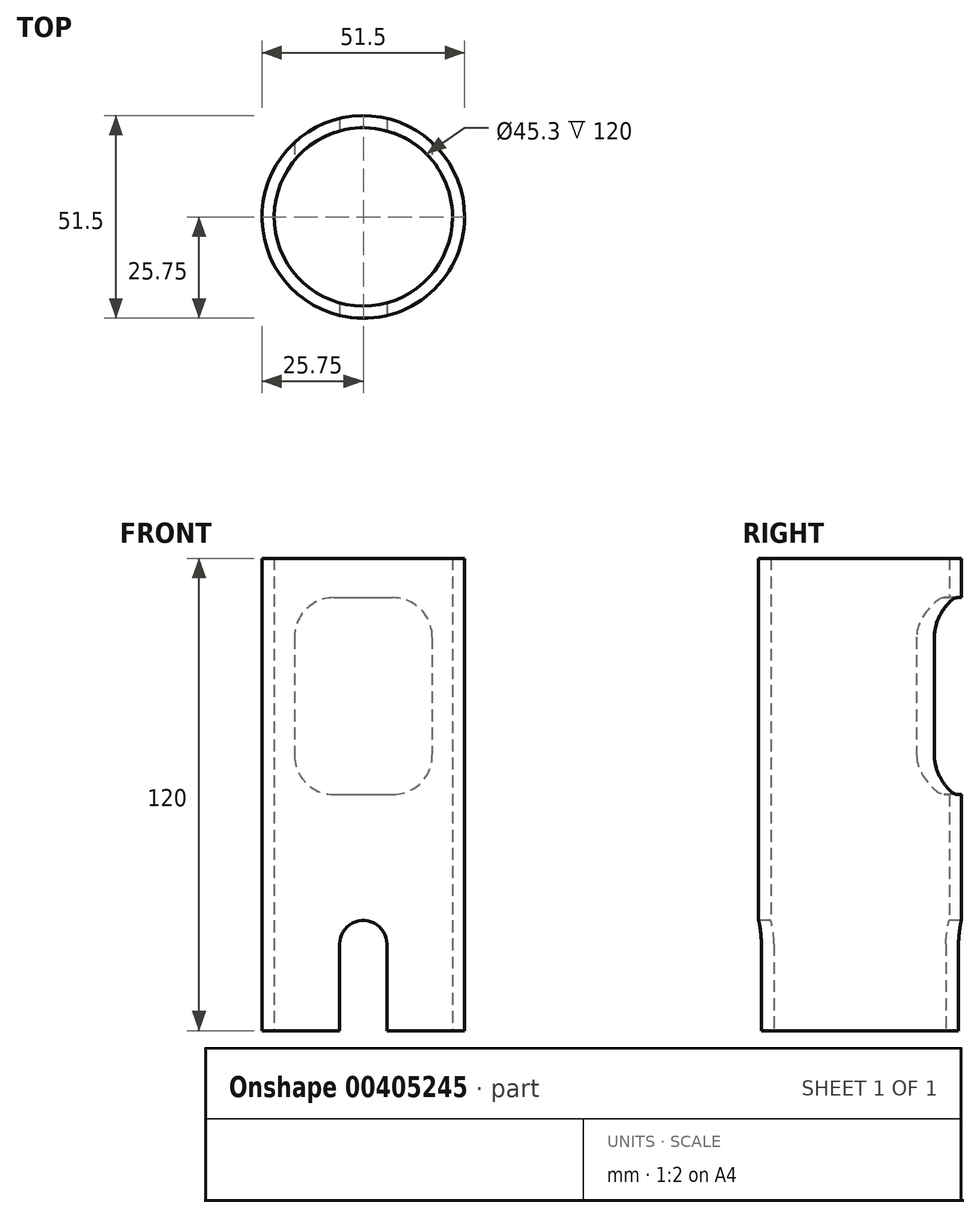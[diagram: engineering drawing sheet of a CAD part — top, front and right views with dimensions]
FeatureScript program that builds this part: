
annotation { "Feature Type Name" : "Feature", "Feature Type Description" : "" }
export const myFeature = defineFeature(function(context is Context, id is Id, definition is map)
    precondition{}
    {
        {
            var Q0;
            Q0=qCreatedBy(makeId("Top.planeOp"),FACE);
            var sketch = newSketch(context, id + "F0", { "sketchPlane" : qUnion([Q0])});
            skCircle(sketch, "E0", {"center": v(0, 0) * mm, "radius": 22.65 * mm});
            skCircle(sketch, "E1", {"center": v(0, 0) * mm, "radius": 25.75 * mm});
            skSolve(sketch);
        }
        {
            var Q0;
            Q0=makeQuery(id+"F0.imprint","IMPRINT",FACE,{"disambiguationData":[TD([[makeQuery(id+"F0.imprint","IMPRINT",EDGE,{"derivedFrom":sQuery(id+"F0.wireOp",EDGE,"E0")}),-1.0]])]});
            extrude(context, id + "F1", {"entities" : qUnion([Q0]), "depth" : 120 * mm});
        }
        {
            var Q0;
            Q0=qCreatedBy(makeId("Front.planeOp"),FACE);
            var sketch = newSketch(context, id + "F2", { "sketchPlane" : qUnion([Q0])});
            skLineSegment(sketch, "E2.bottom", {"start": v(-7.5, 110) * mm, "end": v(7.5, 110) * mm});
            skLineSegment(sketch, "E2.top", {"start": v(-7.5, 60) * mm, "end": v(7.5, 60) * mm});
            skLineSegment(sketch, "E2.left", {"start": v(-17.5, 100) * mm, "end": v(-17.5, 70) * mm});
            skLineSegment(sketch, "E2.right", {"start": v(17.5, 100) * mm, "end": v(17.5, 70) * mm});
            skPoint(sketch, "E3.visualSharp", {"position": v(-17.5, 110) * mm});
            skArc(sketch, "E3.filletArc", {"start": v(-7.5, 110) * mm, "mid": v(-14.57, 107.07) * mm, "end": v(-17.5, 100) * mm});
            skPoint(sketch, "E4.visualSharp", {"position": v(17.5, 110) * mm});
            skArc(sketch, "E4.filletArc", {"start": v(17.5, 100) * mm, "mid": v(14.57, 107.07) * mm, "end": v(7.5, 110) * mm});
            skPoint(sketch, "E5.visualSharp", {"position": v(17.5, 60) * mm});
            skArc(sketch, "E5.filletArc", {"start": v(7.5, 60) * mm, "mid": v(14.57, 62.93) * mm, "end": v(17.5, 70) * mm});
            skPoint(sketch, "E6.visualSharp", {"position": v(-17.5, 60) * mm});
            skArc(sketch, "E6.filletArc", {"start": v(-17.5, 70) * mm, "mid": v(-14.57, 62.93) * mm, "end": v(-7.5, 60) * mm});
            skLineSegment(sketch, "E7", {"start": v(-6, 0) * mm, "end": v(-6, 22) * mm});
            skLineSegment(sketch, "E8", {"start": v(6, 0) * mm, "end": v(6, 22) * mm});
            skLineSegment(sketch, "E9", {"start": v(-6, 0) * mm, "end": v(6, 0) * mm});
            skArc(sketch, "E10", {"start": v(6, 22) * mm, "mid": v(0, 28) * mm, "end": v(-6, 22) * mm});
            skSolve(sketch);
        }
        {
            var Q0;
            Q0=makeQuery(id+"F2.imprint","IMPRINT",FACE,{"disambiguationData":[TD([[makeQuery(id+"F2.imprint","IMPRINT",EDGE,{"derivedFrom":sQuery(id+"F2.wireOp",EDGE,"E2.bottom")}),-1.0]])]});
            extrude(context, id + "F3", {"entities" : qUnion([Q0]), "operationType" : NewBodyOperationType.REMOVE, "endBound" : BoundingType.THROUGH_ALL, "oppositeDirection" : true, "depth" : 61.5 * mm});
        }
        {
            var Q0;
            Q0=makeQuery(id+"F2.imprint","IMPRINT",FACE,{"disambiguationData":[TD([[makeQuery(id+"F2.imprint","IMPRINT",EDGE,{"derivedFrom":sQuery(id+"F2.wireOp",EDGE,"E7")}),-1.0]])]});
            extrude(context, id + "F4", {"entities" : qUnion([Q0]), "operationType" : NewBodyOperationType.REMOVE, "endBound" : BoundingType.SYMMETRIC, "oppositeDirection" : true, "depth" : 60 * mm});
        }
    });
